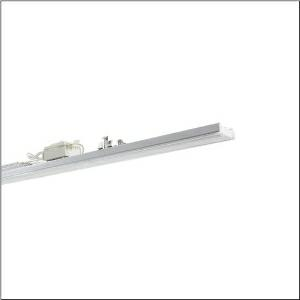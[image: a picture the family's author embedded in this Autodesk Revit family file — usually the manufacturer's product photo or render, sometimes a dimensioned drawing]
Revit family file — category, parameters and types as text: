
# Revit family: licross_11_recessed_ho_51tl1emv4g5s
name_source: partatom
category: Lighting Fixtures
units: mm (PartAtom-declared; Revit-internal decimal feet)

## family parameters
Cut with Voids When Loaded = No
Host = Face
Light Source = No
Part Type = Normal
Room Calculation Point = No
Round Connector Dimension = Use Diameter
Shared = No

## types (1)
- --- (1 x LED, 16830 lm, 89.2 W, 4000K)
    Apparent Load = 89 VA
    CIE Flux Codes = 85 95 99 100 100
    Color Rendering = 80
    Color Temperature = 4000K
    Default Elevation = 1800 mm
    Description = Licross 11 Recessed HO, luminaire insert, of sheet steel, coil coated, white, length: 2.250mm, width: 66mm, height: 67mm, LED rated luminous flux: 16.830lm, light colour: 840, SDCM (Standard Deviation of Colour Matching)MacAdam ≤ 2 SDCM (initial), control gear: ON/OFF Multilumen, with plug, 3-pole, with phase selection, mains connection: 220..240V, AC, 50/60Hz, rated input power: 89W, internal wiring halogen-free, primary light control with lens, of plastic, primary optical cover: cover, of PMMA, light emission: direct distribution, primary light characteristic: symmetric, protection rating (complete): IP40, insulation class (complete): insulation class I (protective earthing), certification: CE, ENEC, VDE, UKCA, protection symbol: D if used in an environment without relevant dust loads with corresponding accessories, impact resistance: IK06, permissible ambient temperature for indoor applications: -35..+35°C, corresponds to IFS (International Featured Standards) requirements for safety and quality in the food industry, reducing of maximum allowable ambient temperature of 5°C with ceiling mounting, The light source and the operating device comply with the requirements of the Ecodesign Regulation (EU) 2019/2020 and are replaceable in accordance with this regulation, packaging unit: 1 piece
    Height = 58 mm
    Lamp = 1 x LED
    Lamp Light Flux = 16830 lm
    Lamp Power = 89.2 W
    Lamp count = 1
    Length = 2250 mm
    Luminous efficacy = 189 lm/W
    Manufacturer = Siteco
    ModVariant = No
    Model = 51TL1EMV4G5S
    Mounting Place = Ceiling
    Mounting Type = Pendant
    Number of Poles = 1
    OnlyDefault = Yes
    Power Factor = 1
    Product Name = Licross 11 Recessed HO
    Product group = luminaire insert | ceiling pendant
    ProductGroupID = 901
    Protection Class = Protection class I
    Protection Degree = IP 40
    RLX_Detail_Level = 1
    RLX_Emergency_Light_Flux = 0 lm
    RLX_Emergency_Type = 0
    RLX_Emergency_Type_DB = No
    RlxData = <blob elided: 27353 chars, md5=6fd3f1a6>
    Socket = socket
    Standby Power = 0 W
    System Light Flux = 16830 lm
    System Power = 89 W
    Type Comments = factory setting: luminous flux: 100 % | (A | C | E) | 210 mA
    Type Image = l_1296930.jpg
    URL = http://relux.com
    VarID = @adj_089239
    Voltage = 0 V
    Weight = 0.00 kg
    Width = 66 mm

## geometry (parser evidence)
native form markers: Blend x4, Sweep x9
no freeform markers — native parametric forms only
